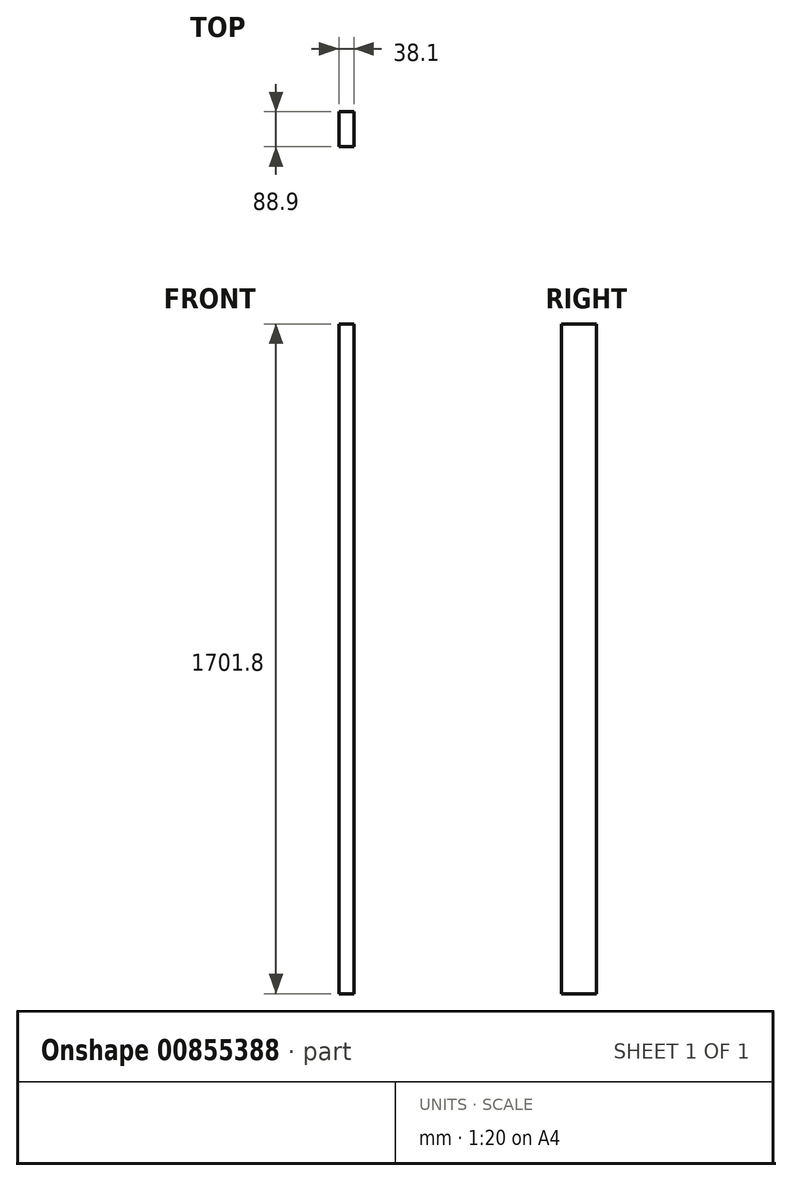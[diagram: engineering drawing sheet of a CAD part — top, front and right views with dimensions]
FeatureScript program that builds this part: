
annotation { "Feature Type Name" : "Feature", "Feature Type Description" : "" }
export const myFeature = defineFeature(function(context is Context, id is Id, definition is map)
    precondition{}
    {
        {
            var Q0;
            Q0=qCreatedBy(makeId("Top.planeOp"),FACE);
            var sketch = newSketch(context, id + "F0", { "sketchPlane" : qUnion([Q0])});
            skLineSegment(sketch, "E0.bottom", {"start": v(0, 0) * mm, "end": v(38.1, 0) * mm});
            skLineSegment(sketch, "E0.top", {"start": v(0, 88.9) * mm, "end": v(38.1, 88.9) * mm});
            skLineSegment(sketch, "E0.left", {"start": v(0, 0) * mm, "end": v(0, 88.9) * mm});
            skLineSegment(sketch, "E0.right", {"start": v(38.1, 0) * mm, "end": v(38.1, 88.9) * mm});
            skSolve(sketch);
        }
        {
            var Q0;
            Q0 = qSketchRegion(id + "F0", true);
            extrude(context, id + "F1", {"entities" : qUnion([Q0]), "depth" : 1701.8 * mm, "offsetDistance" : 25.4 * mm});
        }
    });
